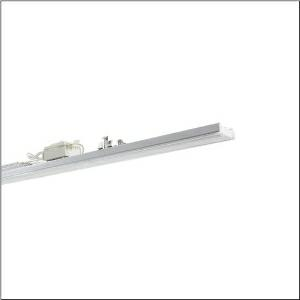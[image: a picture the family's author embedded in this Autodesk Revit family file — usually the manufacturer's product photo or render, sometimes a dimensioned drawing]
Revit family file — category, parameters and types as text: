
# Revit family: licross_r__11_recessed_ho_51tl12cn4c5m_68a2
name_source: partatom
category: Lighting Fixtures
units: mm (PartAtom-declared; Revit-internal decimal feet)

## family parameters
Cut with Voids When Loaded = No
Host = Face
Light Source = No
Part Type = Normal
Room Calculation Point = No
Round Connector Dimension = Use Diameter
Shared = No

## types (1)
- --- (1 x LED, 12740 lm, 66.5 W, 4000K)
    Apparent Load = 67 VA
    CIE Flux Codes = 66 91 98 100 100
    Color Rendering = 80
    Color Temperature = 4000K
    Default Elevation = 1800 mm
    Description = Licross® 11 Recessed HO, luminaire insert, of sheet steel, coil coated, white, length: 1.500mm, width: 66mm, height: 67mm, LED rated luminous flux: 12.740lm, light colour: 840, control gear: ON/OFF Multilumen, CLOi, with plug, 3-pole, with phase selection, mains connection: 220..240V, AC, 50/60Hz, start of lifetime: 67W, end of service life: 75W, halogen-free wiring, primary optical cover: cover, of PMMA, light emission: direct distribution, primary light characteristic: symmetric, protection rating (complete): IP40, insulation class (complete): insulation class I (protective earthing), certification: CE, ENEC, VDE, UKCA, protection symbol: D if used in an environment without relevant dust loads with corresponding accessories, impact resistance: IK06, permissible ambient temperature for indoor applications: -35..+35°C, corresponds to IFS (International Featured Standards) requirements for safety and quality in the food industry, reducing of maximum allowable ambient temperature of 5°C with ceiling mounting, LABS conformity tested according to VDMA 24364:2018-05, packaging unit: 1 piece
    Height = 58 mm
    Lamp = 1 x LED
    Lamp Light Flux = 12740 lm
    Lamp Power = 66.5 W
    Lamp count = 1
    Length = 1500 mm
    Luminous efficacy = 192 lm/W
    Manufacturer = Siteco
    ModVariant = No
    Model = 51TL12CN4C5M
    Mounting Place = Ceiling
    Mounting Type = Pendant
    Number of Poles = 1
    OnlyDefault = Yes
    Power Factor = 1
    Product Name = Licross® 11 Recessed HO
    Product group = luminaire insert
    ProductGroupID = 902
    Protection Class = Protection class I
    Protection Degree = IP 40
    RLX_Detail_Level = 1
    RLX_Emergency_Light_Flux = 0 lm
    RLX_Emergency_Type = 0
    RLX_Emergency_Type_DB = No
    RlxData = <blob elided: 22229 chars, md5=4f8b0a24>
    Socket = socket
    Standby Power = 0 W
    System Light Flux = 12740 lm
    System Power = 67 W
    Type Comments = factory setting: luminous flux: 100 % | (A | C | E) | 156 mA
    Type Image = l_1296930.jpg
    URL = http://relux.com
    VarID = @adj_085058
    Voltage = 0 V
    Weight = 0.00 kg
    Width = 66 mm

## geometry (parser evidence)
native form markers: Blend x4, Sweep x12
no freeform markers — native parametric forms only
